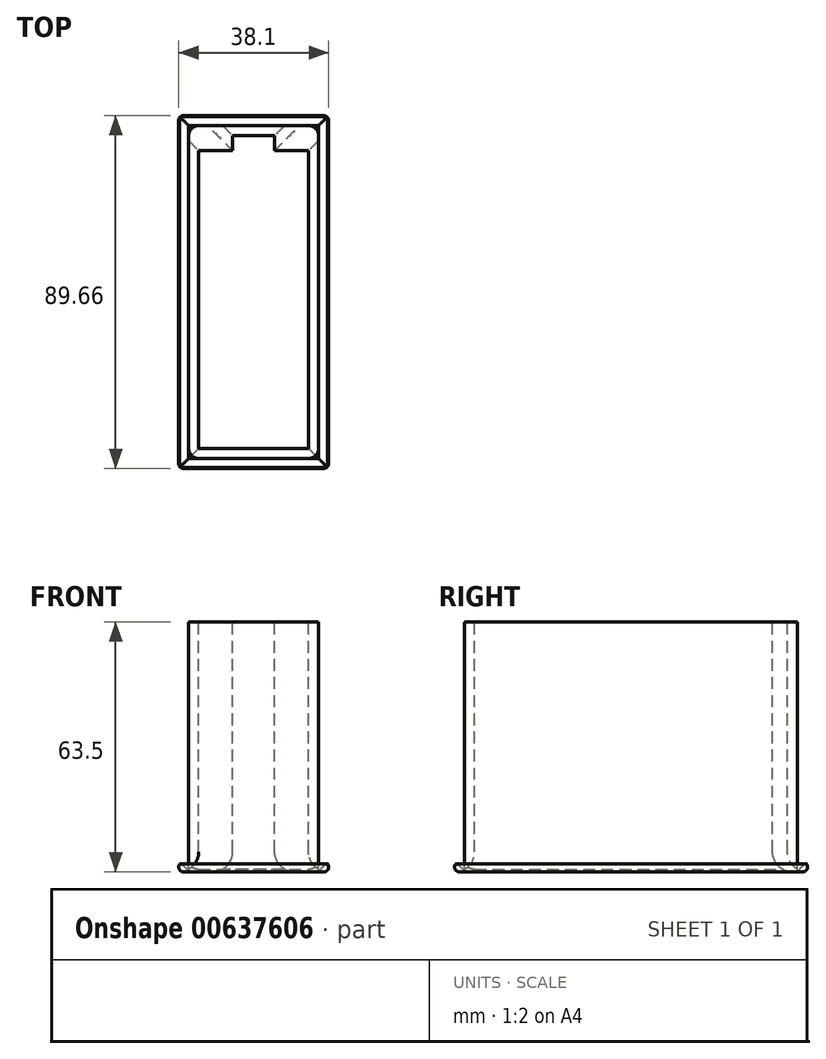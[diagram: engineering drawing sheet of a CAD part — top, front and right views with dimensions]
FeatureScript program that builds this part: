
annotation { "Feature Type Name" : "Feature", "Feature Type Description" : "" }
export const myFeature = defineFeature(function(context is Context, id is Id, definition is map)
    precondition{}
    {
        {
            var Q0;
            Q0=qCreatedBy(makeId("Top.planeOp"),FACE);
            var sketch = newSketch(context, id + "F0", { "sketchPlane" : qUnion([Q0])});
            skLineSegment(sketch, "E0.bottom", {"start": v(16.5, 42.3) * mm, "end": v(-16.51, 42.3) * mm});
            skLineSegment(sketch, "E0.top", {"start": v(16.5, -42.3) * mm, "end": v(-16.5, -42.3) * mm});
            skLineSegment(sketch, "E0.left", {"start": v(16.5, 42.3) * mm, "end": v(16.5, -42.3) * mm});
            skLineSegment(sketch, "E0.right", {"start": v(-16.51, 42.3) * mm, "end": v(-16.51, -42.3) * mm});
            skPoint(sketch, "E0.middle", {"position": v(0, 0) * mm});
            skLineSegment(sketch, "E1.bottom", {"start": v(13.97, 39.75) * mm, "end": v(-13.97, 39.75) * mm});
            skLineSegment(sketch, "E1.top", {"start": v(13.97, -39.75) * mm, "end": v(-13.97, -39.75) * mm});
            skLineSegment(sketch, "E1.left", {"start": v(13.97, 39.75) * mm, "end": v(13.97, -39.75) * mm});
            skLineSegment(sketch, "E1.right", {"start": v(-13.97, 39.75) * mm, "end": v(-13.97, -39.75) * mm});
            skLineSegment(sketch, "E2", {"start": v(-13.97, 35.94) * mm, "end": v(-5.33, 35.94) * mm});
            skLineSegment(sketch, "E3", {"start": v(-5.33, 35.94) * mm, "end": v(-5.33, 39.75) * mm});
            skLineSegment(sketch, "E4", {"start": v(5.33, 39.75) * mm, "end": v(5.33, 35.94) * mm});
            skLineSegment(sketch, "E5", {"start": v(5.33, 35.94) * mm, "end": v(13.97, 35.94) * mm});
            skSolve(sketch);
        }
        {
            var Q0;
            Q0=makeQuery(id+"F0.imprint","IMPRINT",FACE,{"disambiguationData":[TD([[makeQuery(id+"F0.imprint","IMPRINT",EDGE,{"derivedFrom":sQuery(id+"F0.wireOp",EDGE,"E0.bottom")}),1.0]])]});
            var Q1;
            {var subQ4=sQuery(id+"F0.wireOp",EDGE,"E2");Q1=makeQuery(id+"F0.imprint","IMPRINT",FACE,{"disambiguationData":[TD([[makeQuery(id+"F0.imprint","IMPRINT",EDGE,{"derivedFrom":subQ4}),1.0]])]});}
            var Q2;
            {var subQ3=sQuery(id+"F0.wireOp",EDGE,"E4");Q2=makeQuery(id+"F0.imprint","IMPRINT",FACE,{"disambiguationData":[TD([[makeQuery(id+"F0.imprint","IMPRINT",EDGE,{"derivedFrom":subQ3}),1.0]])]});}
            extrude(context, id + "F1", {"entities" : qUnion([Q0, Q1, Q2]), "oppositeDirection" : true, "depth" : 63.5 * mm});
        }
        {
            var Q0;
            Q0=makeQuery(id+"F1.opExtrude","CAP_EDGE",EDGE,{"disambiguationData":[OSD([sQuery(id+"F0.wireOp",EDGE,"E1.bottom")])],"isStart":false});
            var Q1;
            Q1=makeQuery(id+"F1.opExtrude","CAP_EDGE",EDGE,{"disambiguationData":[OSD([sQuery(id+"F0.wireOp",EDGE,"E3")])],"isStart":false});
            var Q2;
            Q2=makeQuery(id+"F1.opExtrude","CAP_EDGE",EDGE,{"disambiguationData":[OSD([sQuery(id+"F0.wireOp",EDGE,"E4")])],"isStart":false});
            var Q3;
            Q3=makeQuery(id+"F1.opExtrude","CAP_EDGE",EDGE,{"disambiguationData":[OSD([sQuery(id+"F0.wireOp",EDGE,"E5")])],"isStart":false});
            var Q4;
            Q4=makeQuery(id+"F1.opExtrude","CAP_EDGE",EDGE,{"disambiguationData":[OSD([sQuery(id+"F0.wireOp",EDGE,"E1.left")])],"isStart":false});
            var Q5;
            Q5=makeQuery(id+"F1.opExtrude","CAP_EDGE",EDGE,{"disambiguationData":[OSD([sQuery(id+"F0.wireOp",EDGE,"E1.right")])],"isStart":false});
            var Q6;
            Q6=makeQuery(id+"F1.opExtrude","CAP_EDGE",EDGE,{"disambiguationData":[OSD([sQuery(id+"F0.wireOp",EDGE,"E1.top")])],"isStart":false});
            var Q7;
            Q7=makeQuery(id+"F1.opExtrude","CAP_EDGE",EDGE,{"disambiguationData":[OSD([sQuery(id+"F0.wireOp",EDGE,"E2")])],"isStart":false});
            fillet(context, id + "F2", {"entities" : qUnion([Q0, Q1, Q2, Q3, Q4, Q5, Q6, Q7]), "radius" : 5.08 * mm, "tangentPropagation" : true, "allowEdgeOverflow" : false});
        }
        {
            var Q0;
            Q0=makeQuery(id+"F2.opFillet","SPLIT",FACE,{"disambiguationData":[OD(1.0)],"derivedFrom":makeQuery(id+"F1.opExtrude","CAP_FACE",FACE,{"disambiguationData":[OSD([sQuery(id+"F0.wireOp",EDGE,"E0.bottom"),sQuery(id+"F0.wireOp",EDGE,"E0.top"),sQuery(id+"F0.wireOp",EDGE,"E0.left"),sQuery(id+"F0.wireOp",EDGE,"E0.right"),sQuery(id+"F0.wireOp",EDGE,"E1.bottom"),sQuery(id+"F0.wireOp",EDGE,"E1.top"),sQuery(id+"F0.wireOp",EDGE,"E1.left"),sQuery(id+"F0.wireOp",EDGE,"E1.right"),sQuery(id+"F0.wireOp",EDGE,"E2"),sQuery(id+"F0.wireOp",EDGE,"E3"),sQuery(id+"F0.wireOp",EDGE,"E4"),sQuery(id+"F0.wireOp",EDGE,"E5")])],"isStart":false})});
            var sketch = newSketch(context, id + "F3", { "sketchPlane" : qUnion([Q0])});
            skLineSegment(sketch, "E6.bottom", {"start": v(19.05, -44.83) * mm, "end": v(-19.05, -44.83) * mm});
            skLineSegment(sketch, "E6.top", {"start": v(19.05, 44.83) * mm, "end": v(-19.05, 44.83) * mm});
            skLineSegment(sketch, "E6.left", {"start": v(19.05, -44.83) * mm, "end": v(19.05, 44.83) * mm});
            skLineSegment(sketch, "E6.right", {"start": v(-19.05, -44.83) * mm, "end": v(-19.05, 44.83) * mm});
            skPoint(sketch, "E6.middle", {"position": v(0, 0) * mm});
            skLineSegment(sketch, "E7.bottom", {"start": v(16.5, 42.3) * mm, "end": v(-16.5, 42.3) * mm});
            skLineSegment(sketch, "E7.top", {"start": v(16.5, -42.3) * mm, "end": v(-16.5, -42.3) * mm});
            skLineSegment(sketch, "E7.left", {"start": v(16.5, 42.3) * mm, "end": v(16.5, -42.3) * mm});
            skLineSegment(sketch, "E7.right", {"start": v(-16.5, 42.3) * mm, "end": v(-16.5, -42.3) * mm});
            skSolve(sketch);
        }
        {
            var Q0;
            Q0=qSketchRegion(id+"F3",true);
            extrude(context, id + "F4", {"entities" : qUnion([Q0]), "oppositeDirection" : true, "depth" : 2.54 * mm});
        }
        {
            var Q0;
            Q0=makeQuery(id+"F4.opExtrude","CAP_EDGE",EDGE,{"disambiguationData":[OSD([sQuery(id+"F3.wireOp",EDGE,"E6.top")])],"isStart":true});
            var Q1;
            Q1=makeQuery(id+"F4.opExtrude","CAP_EDGE",EDGE,{"disambiguationData":[OSD([sQuery(id+"F3.wireOp",EDGE,"E6.left")])],"isStart":true});
            var Q2;
            Q2=makeQuery(id+"F4.opExtrude","CAP_EDGE",EDGE,{"disambiguationData":[OSD([sQuery(id+"F3.wireOp",EDGE,"E6.left")])],"isStart":false});
            var Q3;
            Q3=makeQuery(id+"F4.opExtrude","CAP_EDGE",EDGE,{"disambiguationData":[OSD([sQuery(id+"F3.wireOp",EDGE,"E6.bottom")])],"isStart":true});
            var Q4;
            Q4=makeQuery(id+"F4.opExtrude","CAP_EDGE",EDGE,{"disambiguationData":[OSD([sQuery(id+"F3.wireOp",EDGE,"E6.right")])],"isStart":true});
            var Q5;
            Q5=makeQuery(id+"F4.opExtrude","CAP_EDGE",EDGE,{"disambiguationData":[OSD([sQuery(id+"F3.wireOp",EDGE,"E6.right")])],"isStart":false});
            var Q6;
            Q6=makeQuery(id+"F4.opExtrude","CAP_EDGE",EDGE,{"disambiguationData":[OSD([sQuery(id+"F3.wireOp",EDGE,"E6.top")])],"isStart":false});
            var Q7;
            Q7=makeQuery(id+"F4.opExtrude","SWEPT_EDGE",EDGE,{"disambiguationData":[OSD([sQuery(id+"F3.wireOp",EDGE,"E6.top"),sQuery(id+"F3.wireOp",EDGE,"E6.right")])]});
            var Q8;
            Q8=makeQuery(id+"F4.opExtrude","SWEPT_EDGE",EDGE,{"disambiguationData":[OSD([sQuery(id+"F3.wireOp",EDGE,"E6.top"),sQuery(id+"F3.wireOp",EDGE,"E6.left")])]});
            var Q9;
            Q9=makeQuery(id+"F4.opExtrude","SWEPT_EDGE",EDGE,{"disambiguationData":[OSD([sQuery(id+"F3.wireOp",EDGE,"E6.bottom"),sQuery(id+"F3.wireOp",EDGE,"E6.right")])]});
            var Q10;
            Q10=makeQuery(id+"F4.opExtrude","SWEPT_EDGE",EDGE,{"disambiguationData":[OSD([sQuery(id+"F3.wireOp",EDGE,"E6.bottom"),sQuery(id+"F3.wireOp",EDGE,"E6.left")])]});
            var Q11;
            Q11=makeQuery(id+"F4.opExtrude","CAP_EDGE",EDGE,{"disambiguationData":[OSD([sQuery(id+"F3.wireOp",EDGE,"E6.bottom")])],"isStart":false});
            fillet(context, id + "F5", {"entities" : qUnion([Q0, Q1, Q2, Q3, Q4, Q5, Q6, Q7, Q8, Q9, Q10, Q11]), "radius" : 1.27 * mm, "tangentPropagation" : true, "allowEdgeOverflow" : false});
        }
        {
            var Q0;
            Q0=makeQuery(id+"F4.opExtrude","CAP_EDGE",EDGE,{"disambiguationData":[OSD([sQuery(id+"F3.wireOp",EDGE,"E7.top")])],"isStart":false});
            var Q1;
            Q1=makeQuery(id+"F4.opExtrude","CAP_EDGE",EDGE,{"disambiguationData":[OSD([sQuery(id+"F3.wireOp",EDGE,"E7.left")])],"isStart":false});
            var Q2;
            Q2=makeQuery(id+"F4.opExtrude","CAP_EDGE",EDGE,{"disambiguationData":[OSD([sQuery(id+"F3.wireOp",EDGE,"E7.bottom")])],"isStart":false});
            var Q3;
            Q3=makeQuery(id+"F4.opExtrude","CAP_EDGE",EDGE,{"disambiguationData":[OSD([sQuery(id+"F3.wireOp",EDGE,"E7.right")])],"isStart":false});
            fillet(context, id + "F6", {"entities" : qUnion([Q0, Q1, Q2, Q3]), "radius" : 5.08 * mm, "tangentPropagation" : true, "allowEdgeOverflow" : false});
        }
        {
            var Q0;
            Q0=makeQuery(id+"F1.opExtrude","SWEPT_EDGE",EDGE,{"disambiguationData":[OSD([sQuery(id+"F0.wireOp",EDGE,"E0.top"),sQuery(id+"F0.wireOp",EDGE,"E0.left")])]});
            var Q1;
            Q1=makeQuery(id+"F1.opExtrude","SWEPT_EDGE",EDGE,{"disambiguationData":[OSD([sQuery(id+"F0.wireOp",EDGE,"E0.top"),sQuery(id+"F0.wireOp",EDGE,"E0.right")])]});
            var Q2;
            Q2=makeQuery(id+"F1.opExtrude","SWEPT_EDGE",EDGE,{"disambiguationData":[OSD([sQuery(id+"F0.wireOp",EDGE,"E0.bottom"),sQuery(id+"F0.wireOp",EDGE,"E0.left")])]});
            var Q3;
            Q3=makeQuery(id+"F1.opExtrude","SWEPT_EDGE",EDGE,{"disambiguationData":[OSD([sQuery(id+"F0.wireOp",EDGE,"E0.bottom"),sQuery(id+"F0.wireOp",EDGE,"E0.right")])]});
            fillet(context, id + "F7", {"entities" : qUnion([Q0, Q1, Q2, Q3]), "radius" : 2.54 * mm, "allowEdgeOverflow" : false});
        }
    });
